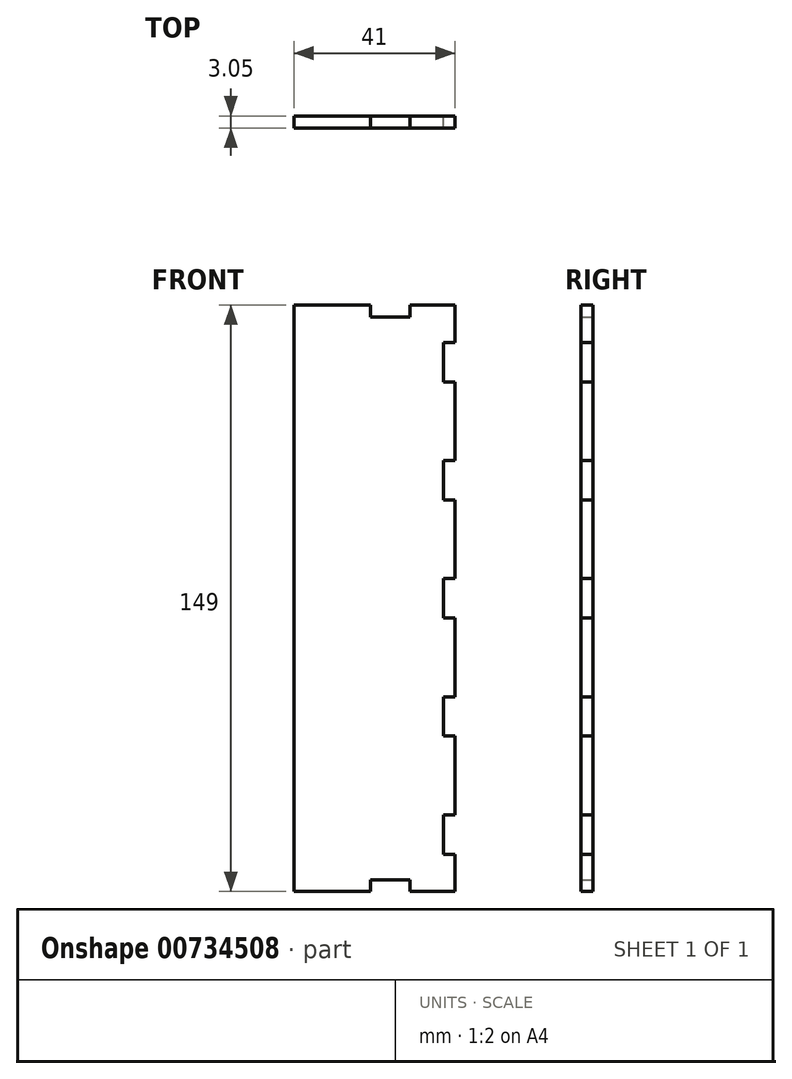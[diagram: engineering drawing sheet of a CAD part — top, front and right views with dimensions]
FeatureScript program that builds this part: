
annotation { "Feature Type Name" : "Feature", "Feature Type Description" : "" }
export const myFeature = defineFeature(function(context is Context, id is Id, definition is map)
    precondition{}
    {
        {
            var Q0;
            Q0=qCreatedBy(makeId("Front.planeOp"),FACE);
            var sketch = newSketch(context, id + "F0", { "sketchPlane" : qUnion([Q0])});
            skLineSegment(sketch, "E0", {"start": v(20.5, -65) * mm, "end": v(20.5, -74.5) * mm});
            skLineSegment(sketch, "E1", {"start": v(20.5, -74.5) * mm, "end": v(9, -74.5) * mm});
            skLineSegment(sketch, "E2", {"start": v(9, -74.5) * mm, "end": v(9, -71.5) * mm});
            skLineSegment(sketch, "E3", {"start": v(9, -71.5) * mm, "end": v(-1, -71.5) * mm});
            skLineSegment(sketch, "E4", {"start": v(-1, -71.5) * mm, "end": v(-1, -74.5) * mm});
            skLineSegment(sketch, "E5", {"start": v(-1, -74.5) * mm, "end": v(-20.5, -74.5) * mm});
            skLineSegment(sketch, "E6", {"start": v(-20.5, -74.5) * mm, "end": v(-20.5, 74.5) * mm});
            skLineSegment(sketch, "E7", {"start": v(-20.5, 74.5) * mm, "end": v(-1, 74.5) * mm});
            skLineSegment(sketch, "E8", {"start": v(-1, 74.5) * mm, "end": v(-1, 71.5) * mm});
            skLineSegment(sketch, "E9", {"start": v(-1, 71.5) * mm, "end": v(9, 71.5) * mm});
            skLineSegment(sketch, "E10", {"start": v(9, 71.5) * mm, "end": v(9, 74.5) * mm});
            skLineSegment(sketch, "E11", {"start": v(9, 74.5) * mm, "end": v(20.5, 74.5) * mm});
            skLineSegment(sketch, "E12", {"start": v(20.5, 74.5) * mm, "end": v(20.5, 65) * mm});
            skLineSegment(sketch, "E13", {"start": v(20.5, 65) * mm, "end": v(17.5, 65) * mm});
            skLineSegment(sketch, "E14", {"start": v(17.5, 65) * mm, "end": v(17.5, 55) * mm});
            skLineSegment(sketch, "E15", {"start": v(17.5, 55) * mm, "end": v(20.5, 55) * mm});
            skLineSegment(sketch, "E16", {"start": v(20.5, 55) * mm, "end": v(20.5, 35) * mm});
            skLineSegment(sketch, "E17", {"start": v(20.5, 35) * mm, "end": v(17.5, 35) * mm});
            skLineSegment(sketch, "E18", {"start": v(17.5, 35) * mm, "end": v(17.5, 25) * mm});
            skLineSegment(sketch, "E19", {"start": v(17.5, 25) * mm, "end": v(20.5, 25) * mm});
            skLineSegment(sketch, "E20", {"start": v(20.5, 25) * mm, "end": v(20.5, 5) * mm});
            skLineSegment(sketch, "E21", {"start": v(20.5, 5) * mm, "end": v(17.5, 5) * mm});
            skLineSegment(sketch, "E22", {"start": v(17.5, 5) * mm, "end": v(17.5, -5) * mm});
            skLineSegment(sketch, "E23", {"start": v(17.5, -5) * mm, "end": v(20.5, -5) * mm});
            skLineSegment(sketch, "E24", {"start": v(20.5, -5) * mm, "end": v(20.5, -25) * mm});
            skLineSegment(sketch, "E25", {"start": v(20.5, -25) * mm, "end": v(17.5, -25) * mm});
            skLineSegment(sketch, "E26", {"start": v(17.5, -25) * mm, "end": v(17.5, -35) * mm});
            skLineSegment(sketch, "E27", {"start": v(17.5, -35) * mm, "end": v(20.5, -35) * mm});
            skLineSegment(sketch, "E28", {"start": v(20.5, -35) * mm, "end": v(20.5, -55) * mm});
            skLineSegment(sketch, "E29", {"start": v(20.5, -55) * mm, "end": v(17.5, -55) * mm});
            skLineSegment(sketch, "E30", {"start": v(17.5, -55) * mm, "end": v(17.5, -65) * mm});
            skLineSegment(sketch, "E31", {"start": v(17.5, -65) * mm, "end": v(20.5, -65) * mm});
            skSolve(sketch);
        }
        {
            var Q0;
            Q0 = qSketchRegion(id + "F0", true);
            extrude(context, id + "F1", {"entities" : qUnion([Q0]), "depth" : 3.05 * mm, "offsetDistance" : 25.4 * mm});
        }
    });
